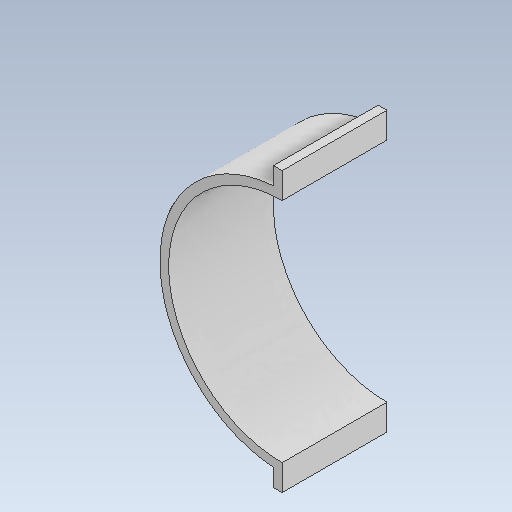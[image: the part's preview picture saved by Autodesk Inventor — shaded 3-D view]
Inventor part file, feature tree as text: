
AUTODESK INVENTOR PART (.ipt)
format: ipt  version: 2020.3 (Build 243373000, 373)  size: 115,200 bytes
history: native  units: in
note: dims shown in document units (in); Inventor stores cm internally (conversion verified against a paired STEP export)
features: other x3, sketch x2, plane x1
ambient origin geometry x8: Origin, YZ Plane, XZ Plane, XY Plane, X Axis, Y Axis, Z Axis, Center Point
bodies: Solid1 (feature_tree)
feature tree (6):
  other  "tubeBracket.ipt"
  other  "Solid1::tubeBracket.ipt"
  other  "TaggingFeature1"
  sketch  "Sketch1"  dims[d0=0.3937in]
  sketch  "Sketch2"
  plane  "Work Plane1"
